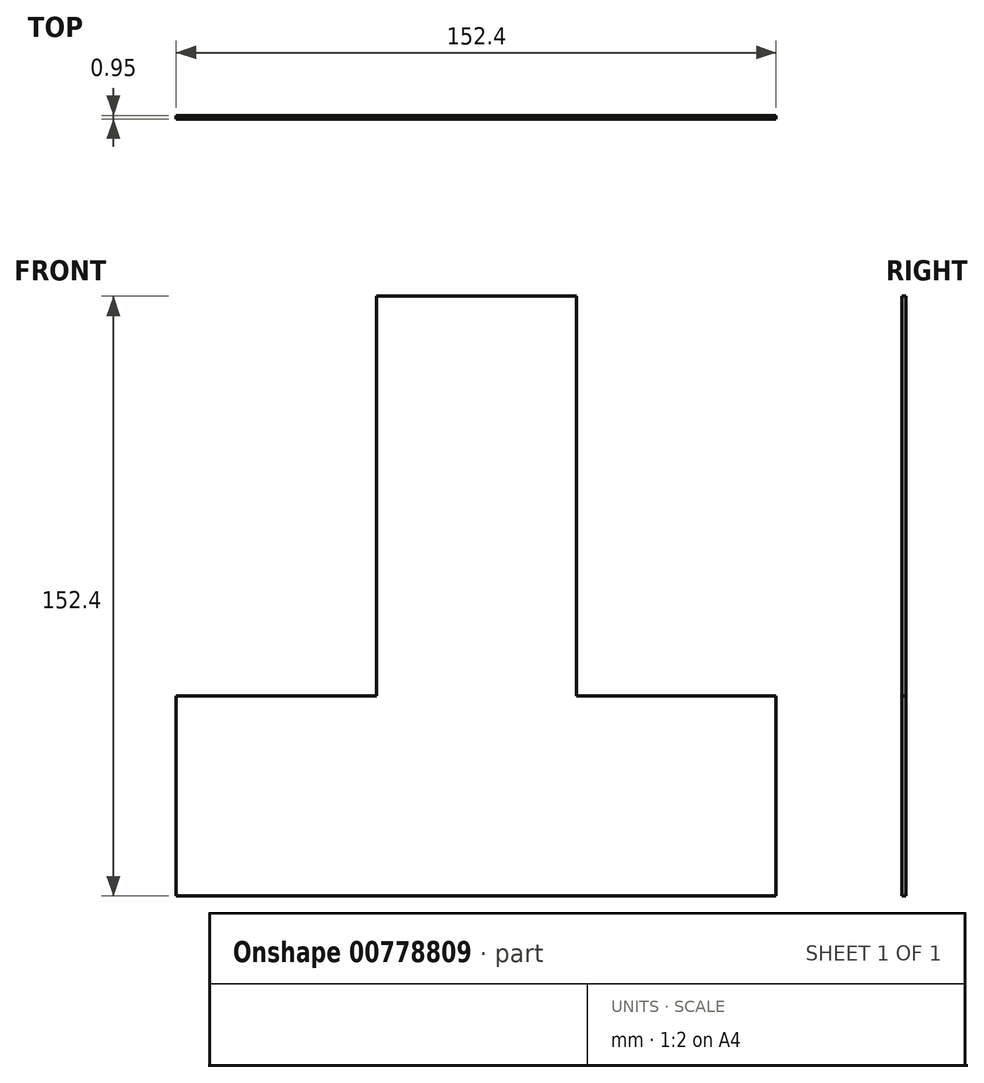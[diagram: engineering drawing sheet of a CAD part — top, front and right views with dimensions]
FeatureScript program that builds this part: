
annotation { "Feature Type Name" : "Feature", "Feature Type Description" : "" }
export const myFeature = defineFeature(function(context is Context, id is Id, definition is map)
    precondition{}
    {
        {
            var Q0;
            Q0=qCreatedBy(makeId("Front.planeOp"),FACE);
            var sketch = newSketch(context, id + "F0", { "sketchPlane" : qUnion([Q0])});
            skLineSegment(sketch, "E0.top", {"start": v(0, 101.6) * mm, "end": v(50.8, 101.6) * mm});
            skLineSegment(sketch, "E0.left", {"start": v(0, 0) * mm, "end": v(0, 101.6) * mm});
            skLineSegment(sketch, "E0.right", {"start": v(50.8, 0) * mm, "end": v(50.8, 101.6) * mm});
            skLineSegment(sketch, "E1", {"start": v(0, 0) * mm, "end": v(-50.8, 0) * mm});
            skLineSegment(sketch, "E2", {"start": v(-50.8, 0) * mm, "end": v(-50.8, -50.8) * mm});
            skLineSegment(sketch, "E3", {"start": v(-50.8, -50.8) * mm, "end": v(101.6, -50.8) * mm});
            skLineSegment(sketch, "E4", {"start": v(101.6, -50.8) * mm, "end": v(101.6, 0) * mm});
            skLineSegment(sketch, "E5", {"start": v(101.6, 0) * mm, "end": v(50.8, 0) * mm});
            skSolve(sketch);
        }
        {
            var Q0;
            Q0=makeQuery(id+"F0.imprint","IMPRINT",FACE,{"disambiguationData":[TD([[makeQuery(id+"F0.imprint","IMPRINT",EDGE,{"derivedFrom":sQuery(id+"F0.wireOp",EDGE,"E0.top")}),-1.0]])]});
            extrude(context, id + "F1", {"entities" : qUnion([Q0]), "depth" : 0.95 * mm, "offsetDistance" : 25.4 * mm});
        }
    });
